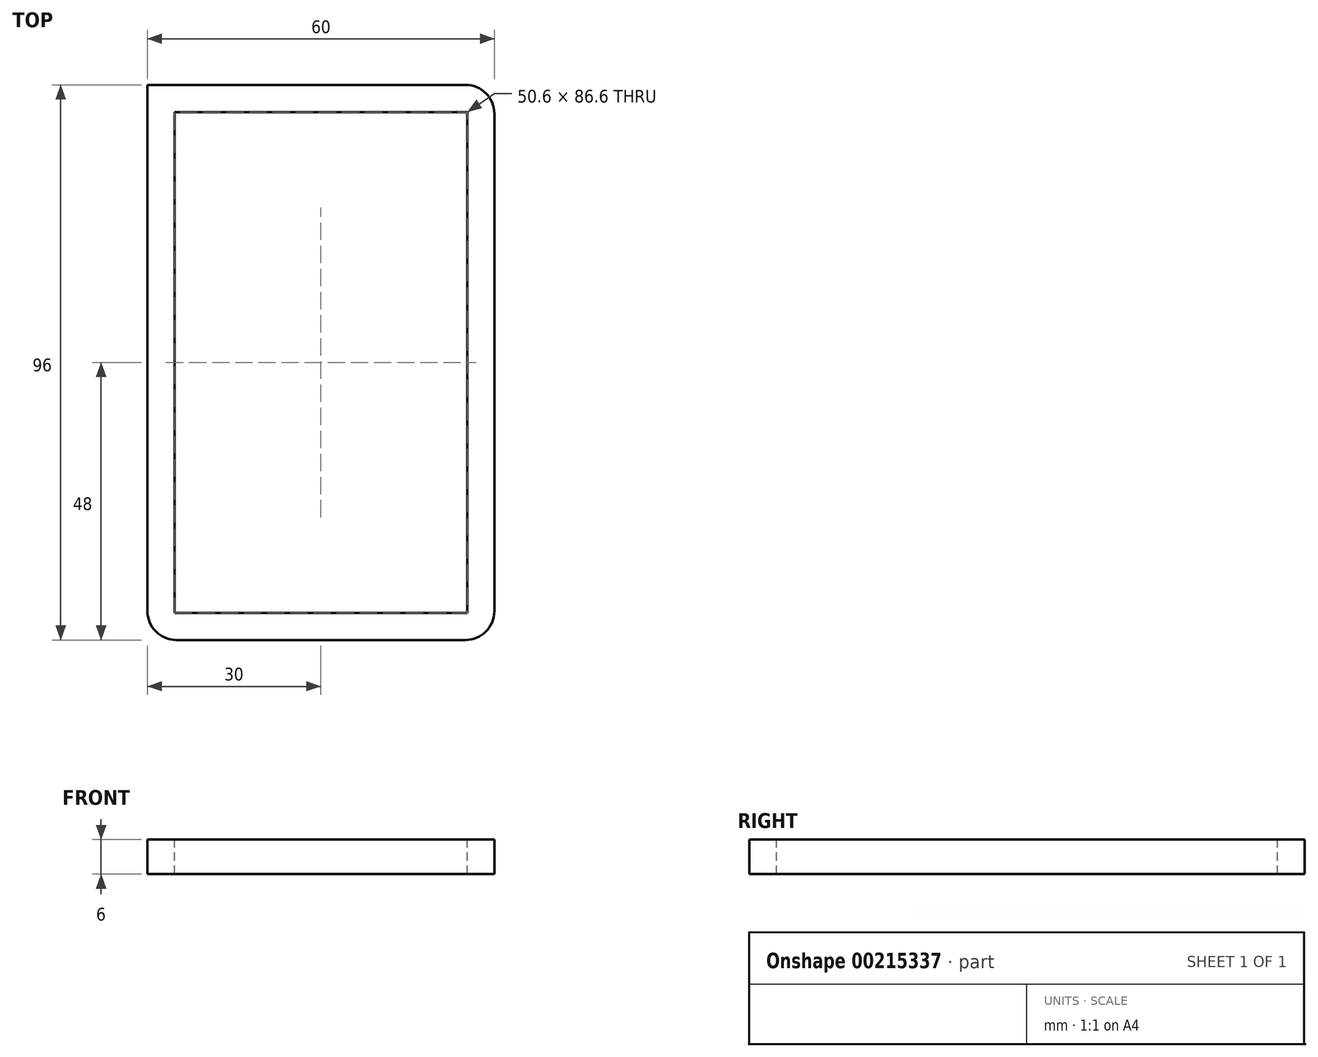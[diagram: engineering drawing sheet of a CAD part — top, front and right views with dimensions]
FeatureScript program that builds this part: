
annotation { "Feature Type Name" : "Feature", "Feature Type Description" : "" }
export const myFeature = defineFeature(function(context is Context, id is Id, definition is map)
    precondition{}
    {
        {
            var Q0;
            Q0=qCreatedBy(makeId("Top.planeOp"),FACE);
            var sketch = newSketch(context, id + "F0", { "sketchPlane" : qUnion([Q0])});
            skPoint(sketch, "E0.middle", {"position": v(0, 0) * mm});
            skCircle(sketch, "E1", {"center": v(-22, 40) * mm, "radius": 1.5 * mm});
            skCircle(sketch, "E2", {"center": v(22, 40) * mm, "radius": 1.5 * mm});
            skCircle(sketch, "E3", {"center": v(-22, -36.08) * mm, "radius": 1.5 * mm});
            skCircle(sketch, "E4", {"center": v(22, -36.08) * mm, "radius": 1.5 * mm});
            skLineSegment(sketch, "E5.bottom", {"start": v(25, -48) * mm, "end": v(-25, -48) * mm});
            skLineSegment(sketch, "E5.top", {"start": v(25, 48) * mm, "end": v(-27, 48) * mm});
            skLineSegment(sketch, "E5.left", {"start": v(30, -43) * mm, "end": v(30, 43) * mm});
            skLineSegment(sketch, "E5.right", {"start": v(-30, -43) * mm, "end": v(-30, 43) * mm});
            skPoint(sketch, "E6.visualSharp", {"position": v(-30, 48) * mm});
            skPoint(sketch, "E7.visualSharp", {"position": v(30, 48) * mm});
            skLineSegment(sketch, "E8.top", {"start": v(-30, 48) * mm, "end": v(-27, 48) * mm});
            skLineSegment(sketch, "E8.left", {"start": v(-30, 43) * mm, "end": v(-30, 48) * mm});
            skArc(sketch, "E9.filletArc", {"start": v(30, 43) * mm, "mid": v(28.54, 46.54) * mm, "end": v(25, 48) * mm});
            skPoint(sketch, "E10.visualSharp", {"position": v(30, -48) * mm});
            skArc(sketch, "E10.filletArc", {"start": v(25, -48) * mm, "mid": v(28.54, -46.54) * mm, "end": v(30, -43) * mm});
            skPoint(sketch, "E11.visualSharp", {"position": v(-30, -48) * mm});
            skArc(sketch, "E11.filletArc", {"start": v(-30, -43) * mm, "mid": v(-28.54, -46.54) * mm, "end": v(-25, -48) * mm});
            skSolve(sketch);
        }
        {
            var Q0;
            Q0=qSketchRegion(id+"F0",true);
            extrude(context, id + "F1", {"entities" : qUnion([Q0]), "depth" : 6 * mm});
        }
        {
            var Q0;
            Q0=makeQuery(id+"F1.opExtrude","CAP_FACE",FACE,{"disambiguationData":[OSD([sQuery(id+"F0.wireOp",EDGE,"E1"),sQuery(id+"F0.wireOp",EDGE,"E2"),sQuery(id+"F0.wireOp",EDGE,"E3"),sQuery(id+"F0.wireOp",EDGE,"E4"),sQuery(id+"F0.wireOp",EDGE,"E5.bottom"),sQuery(id+"F0.wireOp",EDGE,"E5.top"),sQuery(id+"F0.wireOp",EDGE,"E5.left"),sQuery(id+"F0.wireOp",EDGE,"E5.right")])],"isStart":false});
            var sketch = newSketch(context, id + "F2", { "sketchPlane" : qUnion([Q0])});
            skLineSegment(sketch, "E12.bottom", {"start": v(-25.3, 43.3) * mm, "end": v(25.3, 43.3) * mm});
            skLineSegment(sketch, "E12.top", {"start": v(-25.3, -43.3) * mm, "end": v(25.3, -43.3) * mm});
            skLineSegment(sketch, "E12.left", {"start": v(-25.3, 43.3) * mm, "end": v(-25.3, -43.3) * mm});
            skLineSegment(sketch, "E12.right", {"start": v(25.3, 43.3) * mm, "end": v(25.3, -43.3) * mm});
            skPoint(sketch, "E12.middle", {"position": v(0, 0) * mm});
            skSolve(sketch);
        }
        {
            var Q0;
            Q0=qSketchRegion(id+"F2",true);
            extrude(context, id + "F3", {"entities" : qUnion([Q0]), "operationType" : NewBodyOperationType.REMOVE, "oppositeDirection" : true, "depth" : 6 * mm});
        }
    });
